# Revit family: NBS_Senator_MeetingPods_HavenPods_MidHeight_Solo
name_source: partatom
category: Furniture
revit_build: Autodesk Revit 2017 (Build: 20181011_1645(x64)
units: mm (PartAtom-declared; Revit-internal decimal feet)

## family parameters
Always vertical = Yes
Cut with Voids When Loaded = No
Room Calculation Point = No
Shared = No
Work Plane-Based = No

## types (2) — shared parameters
AssetType = Movable
ContrastOuterPanelMaterial = NBS_Concept
Description = Compact single person workspace
DurationUnit = year
ExpectedLife = 10
Features = Internal steel frame with multi layered foam construction, outer vertical panels upholstered in camira blazer fabric (two-tone is standard), quick release panel connector system, levelling adjusters, integral work surface, integral work surface power and data module, incorporating; 1 x 3.15 amp power socket, powered USB and cat 6 data with 1.5 m supply leads, integral under work surface vertical cable management, , optional feature: two-tone upholstery on integrated seat units , accessory: HAPCH coat hanger , accessory: HAPNP name plate, accessory: HAPWBA2 A2 magnetic dry wipe board with hanger, accessory: HAPWBA3 A3 magnetic dry wipe board with hanger,
FrameMaterial = NBS_Concept
IfcExportAs = IfcFurnitureType
IfcExportType = USERDEFINED
InnerPanelMaterial = NBS_Concept
IntegralAccessories = Coat hanger, name plate, A2 magnetic dry wipe board with hanger, A3 magnetic dry wipe board with hanger
IsBuiltIn = No
ManufacturerName = Senator
ManufacturerURL = http://www.thesenatorgroup.com
ModelReference = Haven Pods Mid Height Solo
NBSCertification = www.nationalbimlibrary.com/cert/acbeogns
NBSDescription = Meeting pods
NBSReference = 45-35-20/342
NominalDepth = 1700 mm
NominalHeight = 1400 mm  [stored 4.59318 ft]
NominalLength = 1400 mm  [stored 4.59318 ft]
NominalWidth = 1400 mm  [stored 4.59318 ft]
OuterPanelMaterial = NBS_Concept
ProductInformation = http://www.thesenatorgroup.com
Size = 1700 x 1400 x 1400 mm
Status = New
Style = Workspace pod
SustainabilityPerformance = http://www.thesenatorgroup.com
Uniclass2015Code = Pr_40_50_12_53
Uniclass2015Title = Meeting pods
Uniclass2015Version = Products v1.12
Version = 1
WarrantyDescription = Senator warrants that its manufactured products are free from manufacturing defects - in materials or workmanship - for a period of ten (10) years on Senator Seating ranges; and fifteen (15) years on Senator Desking ranges
WarrantyDurationParts = 10
WarrantyDurationUnit = year

## per-type parameters (varying)
| type | BIMObjectName | Category | IsLeftHand | IsRightHand | Name |
| HAPDS14L | NBS_Senator_MeetingPods_HavenPods_MidHeightSolo_HAPDS14L | Pr_40_50_12_53: Meeting pods | Yes | No | MeetingPods_HavenPodsMidHeightSolo_HAPDS14L_Senator |
| HAPDS14R | NBS_Senator_MeetingPods_HavenPods_MidHeightSolo_HAPDS14R | Pr_40_50_12_53:Meeting pods | No | Yes | MeetingPods_HavenPodsMidHeightSolo_HAPDS14R_Senator |

note: column(s) folded — value = type name in every type: ModelNumber

note: [stored X ft] marks values corroborated as IEEE doubles in the binary element streams (Revit-internal decimal feet)

## geometry (parser evidence)
native form markers: Sweep x6
no freeform markers — native parametric forms only
